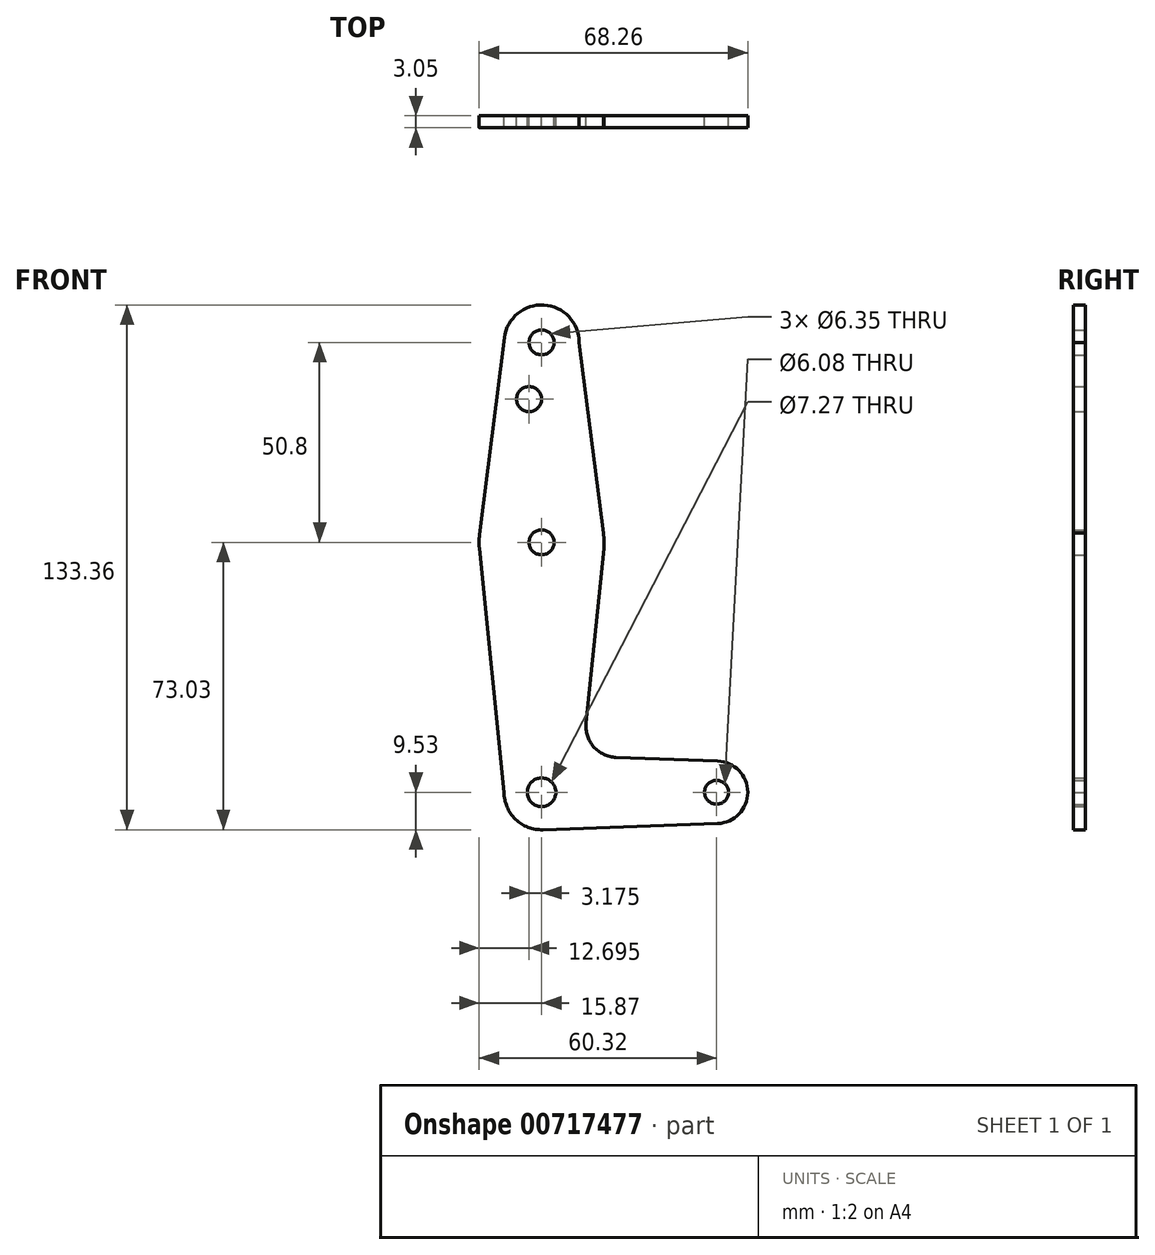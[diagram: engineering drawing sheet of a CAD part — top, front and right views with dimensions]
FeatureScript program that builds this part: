
annotation { "Feature Type Name" : "Feature", "Feature Type Description" : "" }
export const myFeature = defineFeature(function(context is Context, id is Id, definition is map)
    precondition{}
    {
        {
            var Q0;
            Q0=qCreatedBy(makeId("Front.planeOp"),FACE);
            var sketch = newSketch(context, id + "F0", { "sketchPlane" : qUnion([Q0])});
            skCircle(sketch, "E0", {"center": v(0, 114.3) * mm, "radius": 9.53 * mm});
            skCircle(sketch, "E1", {"center": v(0, 63.5) * mm, "radius": 15.88 * mm});
            skCircle(sketch, "E2", {"center": v(0, 0) * mm, "radius": 9.53 * mm});
            skLineSegment(sketch, "E3", {"start": v(0, 114.3) * mm, "end": v(0, 0) * mm});
            skLineSegment(sketch, "E4", {"start": v(0, 0) * mm, "end": v(44.45, 0) * mm});
            skCircle(sketch, "E5", {"center": v(44.45, 0) * mm, "radius": 7.94 * mm});
            skLineSegment(sketch, "E6", {"start": v(-9.45, 115.5) * mm, "end": v(-15.75, 65.48) * mm});
            skLineSegment(sketch, "E7", {"start": v(-15.8, 61.9) * mm, "end": v(-9.52, 0) * mm});
            skLineSegment(sketch, "E8", {"start": v(11.3, 17.6) * mm, "end": v(15.8, 61.9) * mm});
            skLineSegment(sketch, "E9", {"start": v(0, -9.53) * mm, "end": v(44.73, -7.93) * mm});
            skLineSegment(sketch, "E10", {"start": v(18.93, 8.85) * mm, "end": v(44.73, 7.93) * mm});
            skLineSegment(sketch, "E11", {"start": v(9.53, 114.3) * mm, "end": v(15.8, 65.1) * mm});
            skCircle(sketch, "E12", {"center": v(0, 114.3) * mm, "radius": 3.18 * mm});
            skCircle(sketch, "E13", {"center": v(-3.17, 99.89) * mm, "radius": 3.18 * mm});
            skCircle(sketch, "E14", {"center": v(0, 0) * mm, "radius": 3.64 * mm});
            skCircle(sketch, "E15", {"center": v(44.45, 0) * mm, "radius": 3.04 * mm});
            skArc(sketch, "E16.filletArc", {"start": v(11.3, 17.6) * mm, "mid": v(13.22, 11.57) * mm, "end": v(18.93, 8.85) * mm});
            skCircle(sketch, "E17", {"center": v(0, 63.5) * mm, "radius": 3.18 * mm});
            skSolve(sketch);
        }
        {
            var Q0;
            Q0 = qSketchRegion(id + "F0", true);
            var Q1;
            {var subQ0=sQuery(id+"F0.wireOp",EDGE,"E3");var subQ1=sQuery(id+"F0.wireOp",EDGE,"E2");var subQ2=makeQuery(id+"F0.imprint","INTERSECT",VERTEX,{"derivedFrom":[subQ1,subQ0]});Q1=makeQuery(id+"F0.imprint","IMPRINT",FACE,{"disambiguationData":[TD([[makeQuery(id+"F0.imprint","IMPRINT",EDGE,{"disambiguationData":[TD([[subQ2,1.0]])],"derivedFrom":subQ1}),1.0]])]});}
            extrude(context, id + "F1", {"entities" : qUnion([Q0, Q1]), "depth" : 3.05 * mm, "offsetDistance" : 25.4 * mm});
        }
    });
